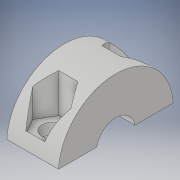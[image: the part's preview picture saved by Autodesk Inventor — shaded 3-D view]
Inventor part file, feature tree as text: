
AUTODESK INVENTOR PART (.ipt)
format: ipt  version: 2019 (Build 230136000, 136)  size: 172,544 bytes
history: native  units: mm
features: sketch x5, extrude x4, plane x2, hole x1, mirror x1
ambient origin geometry x8: Origin, YZ Plane, XZ Plane, XY Plane, X Axis, Y Axis, Z Axis, Center Point
bodies: Solid1 (feature_tree)
feature tree (13):
  extrude  "Extrusion1"  Depth=20.0mm
  extrude  "Extrusion3"  Depth=3.490659mm
  plane  "Work Plane1"
  extrude  "Extrusion4"  Depth=9.0mm
  plane  "Work Plane2"
  hole  "Hole1"  [1 undecoded]
  mirror  "Mirror1"
  extrude  "Extrusion6"  Depth=7.5mm TaperAngle=0.0deg
  sketch  "Sketch1"  dims[d0=6.75mm d1=20.0mm]
  sketch  "Sketch3"  dims[d2=13.962634mm d3=3.490659mm]
  sketch  "Sketch4"  dims[d4=9.0mm d5=0.0mm d9=15.0mm]
  sketch  "Sketch5"  dims[d10=0.5mm d11=0.0mm d12=10.0mm]
  sketch  "Sketch8"  dims[d13=5.75mm d14=7.5mm d15=0.0mm d16=-20.0mm d17=3.5mm d18=6.0mm d19=6.0mm d20=7.5mm d21=90.0deg d22=8.0mm d23=0.0mm d29=10.0mm d30=0.0mm]
note: 1 required parameter value undecoded (feature->parameter linkage not recoverable at this tier; creation-order binding heuristic only, values carry confidence <= 0.55)
